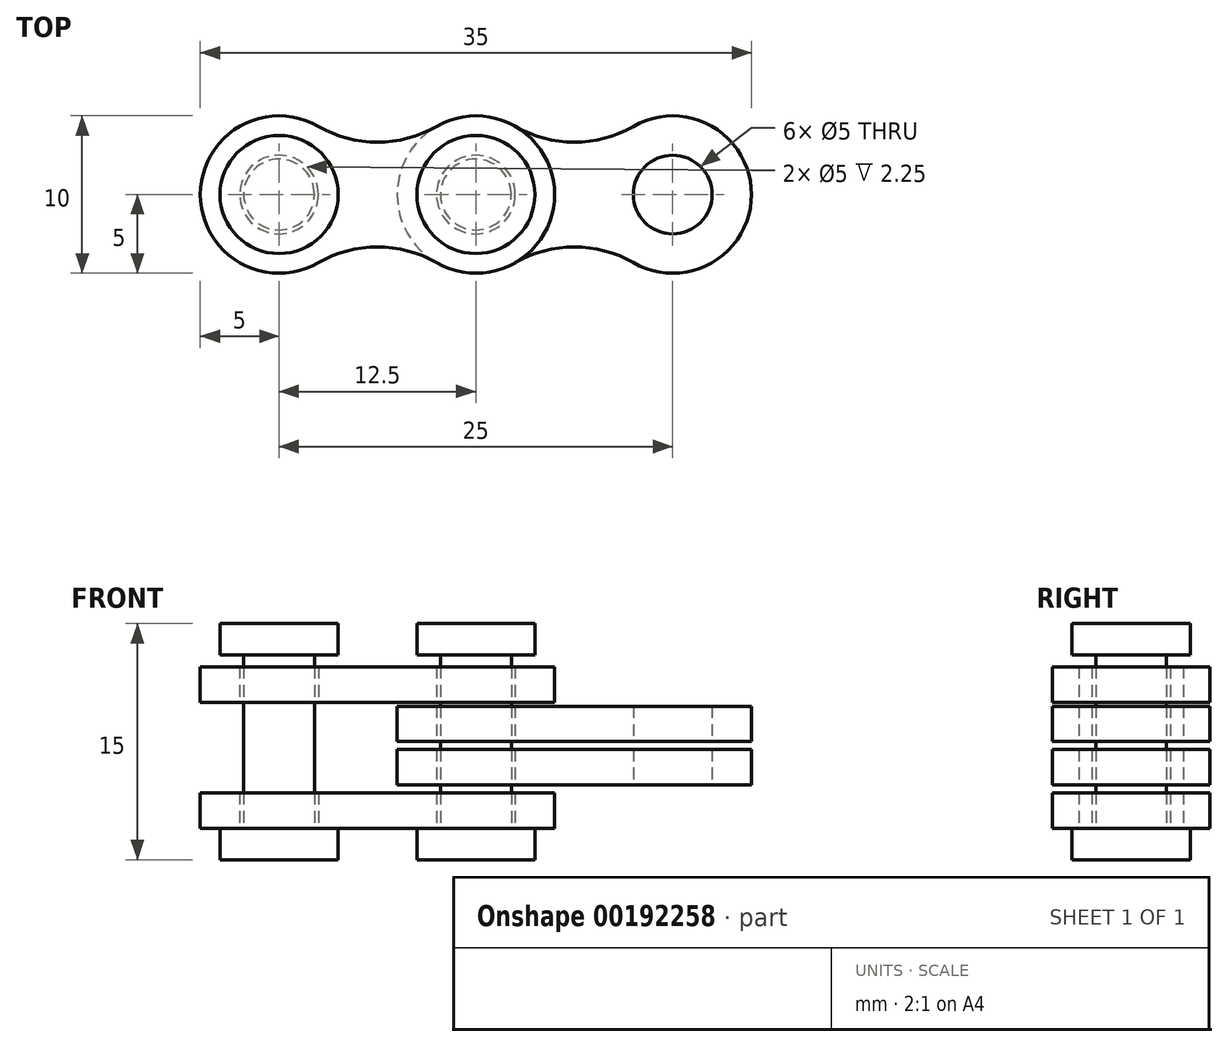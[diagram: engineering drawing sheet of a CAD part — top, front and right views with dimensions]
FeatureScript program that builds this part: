
annotation { "Feature Type Name" : "Feature", "Feature Type Description" : "" }
export const myFeature = defineFeature(function(context is Context, id is Id, definition is map)
    precondition{}
    {
        {
            var Q0;
            Q0=qCreatedBy(makeId("Top.planeOp"),FACE);
            var sketch = newSketch(context, id + "F0", { "sketchPlane" : qUnion([Q0])});
            skCircle(sketch, "E0", {"center": v(0, 0) * mm, "radius": 2.5 * mm});
            skCircle(sketch, "E1", {"center": v(12.5, 0) * mm, "radius": 2.5 * mm});
            skArc(sketch, "E2", {"start": v(2.5, 4.33) * mm, "mid": v(-5, 0) * mm, "end": v(2.5, -4.33) * mm});
            skArc(sketch, "E3", {"start": v(10, -4.33) * mm, "mid": v(17.5, 0) * mm, "end": v(10, 4.33) * mm});
            skArc(sketch, "E4", {"start": v(2.5, 4.33) * mm, "mid": v(6.25, 3.33) * mm, "end": v(10, 4.33) * mm});
            skArc(sketch, "E5", {"start": v(10, -4.33) * mm, "mid": v(6.25, -3.33) * mm, "end": v(2.5, -4.33) * mm});
            skSolve(sketch);
        }
        {
            var Q0;
            Q0=makeQuery(id+"F0.imprint","IMPRINT",FACE,{"disambiguationData":[TD([[makeQuery(id+"F0.imprint","IMPRINT",EDGE,{"derivedFrom":sQuery(id+"F0.wireOp",EDGE,"E0")}),-1.0]])]});
            extrude(context, id + "F1", {"entities" : qUnion([Q0]), "depth" : 2.25 * mm});
        }
        {
            var Q0;
            Q0=qCreatedBy(makeId("Top.planeOp"),FACE);
            var sketch = newSketch(context, id + "F2", { "sketchPlane" : qUnion([Q0])});
            skCircle(sketch, "E6", {"center": v(0, 0) * mm, "radius": 2.25 * mm});
            skCircle(sketch, "E7", {"center": v(12.5, 0) * mm, "radius": 2.25 * mm});
            skSolve(sketch);
        }
        {
            var Q0;
            Q0=makeQuery(id+"F2.imprint","IMPRINT",FACE,{"disambiguationData":[TD([[makeQuery(id+"F2.imprint","IMPRINT",EDGE,{"derivedFrom":sQuery(id+"F2.wireOp",EDGE,"E6")}),1.0]])]});
            var Q1;
            Q1=makeQuery(id+"F2.imprint","IMPRINT",FACE,{"disambiguationData":[TD([[makeQuery(id+"F2.imprint","IMPRINT",EDGE,{"derivedFrom":sQuery(id+"F2.wireOp",EDGE,"E7")}),1.0]])]});
            extrude(context, id + "F3", {"entities" : qUnion([Q0, Q1]), "depth" : 11 * mm});
        }
        {
            var Q0;
            Q0=makeQuery(id+"F1.opExtrude","SWEPT_BODY",BODY,{"disambiguationData":[OSD([sQuery(id+"F0.wireOp",EDGE,"E0"),sQuery(id+"F0.wireOp",EDGE,"E1"),sQuery(id+"F0.wireOp",EDGE,"E2"),sQuery(id+"F0.wireOp",EDGE,"E3"),sQuery(id+"F0.wireOp",EDGE,"E4"),sQuery(id+"F0.wireOp",EDGE,"E5")])]});
            transform(context, id + "F4", {"entities" : qUnion([Q0]), "transformType" : TransformType.TRANSLATION_3D, "dx" : 0 * mm, "dy" : 0 * mm, "dz" : 8 * mm, "makeCopy" : true});
        }
        {
            var Q0;
            Q0=makeQuery(id+"F1.opExtrude","SWEPT_BODY",BODY,{"disambiguationData":[OSD([sQuery(id+"F0.wireOp",EDGE,"E0"),sQuery(id+"F0.wireOp",EDGE,"E1"),sQuery(id+"F0.wireOp",EDGE,"E2"),sQuery(id+"F0.wireOp",EDGE,"E3"),sQuery(id+"F0.wireOp",EDGE,"E4"),sQuery(id+"F0.wireOp",EDGE,"E5")])]});
            transform(context, id + "F5", {"entities" : qUnion([Q0]), "transformType" : TransformType.TRANSLATION_3D, "dx" : 12.5 * mm, "dy" : 0 * mm, "dz" : 2.75 * mm, "makeCopy" : true});
        }
        {
            var Q0;
            Q0=makeQuery(id+"F5.opPattern","COPY",BODY,{"derivedFrom":makeQuery(id+"F1.opExtrude","SWEPT_BODY",BODY,{"disambiguationData":[OSD([sQuery(id+"F0.wireOp",EDGE,"E0"),sQuery(id+"F0.wireOp",EDGE,"E1"),sQuery(id+"F0.wireOp",EDGE,"E2"),sQuery(id+"F0.wireOp",EDGE,"E3"),sQuery(id+"F0.wireOp",EDGE,"E4"),sQuery(id+"F0.wireOp",EDGE,"E5")])]}),"instanceName":"1"});
            transform(context, id + "F6", {"entities" : qUnion([Q0]), "transformType" : TransformType.TRANSLATION_3D, "dx" : 0 * mm, "dy" : 0 * mm, "dz" : 2.75 * mm, "makeCopy" : true});
        }
        {
            var Q0;
            Q0=makeQuery(id+"F3.opExtrude","CAP_FACE",FACE,{"disambiguationData":[OSD([sQuery(id+"F2.wireOp",EDGE,"E6")])],"isStart":false});
            var sketch = newSketch(context, id + "F7", { "sketchPlane" : qUnion([Q0])});
            skCircle(sketch, "E8", {"center": v(0, 0) * mm, "radius": 3.75 * mm});
            skCircle(sketch, "E9", {"center": v(12.5, 0) * mm, "radius": 3.75 * mm});
            skSolve(sketch);
        }
        {
            var Q0;
            Q0 = qSketchRegion(id + "F7", true);
            extrude(context, id + "F8", {"entities" : qUnion([Q0]), "operationType" : NewBodyOperationType.ADD, "depth" : 2 * mm});
        }
        {
            var Q0;
            Q0=makeQuery(id+"F3.opExtrude","CAP_FACE",FACE,{"disambiguationData":[OSD([sQuery(id+"F2.wireOp",EDGE,"E6")])],"isStart":true});
            var sketch = newSketch(context, id + "F9", { "sketchPlane" : qUnion([Q0])});
            skCircle(sketch, "E10", {"center": v(0, 0) * mm, "radius": 3.75 * mm});
            skCircle(sketch, "E11", {"center": v(12.5, 0) * mm, "radius": 3.75 * mm});
            skSolve(sketch);
        }
        {
            var Q0;
            Q0 = qSketchRegion(id + "F9", true);
            extrude(context, id + "F10", {"entities" : qUnion([Q0]), "operationType" : NewBodyOperationType.ADD, "depth" : 2 * mm});
        }
    });
